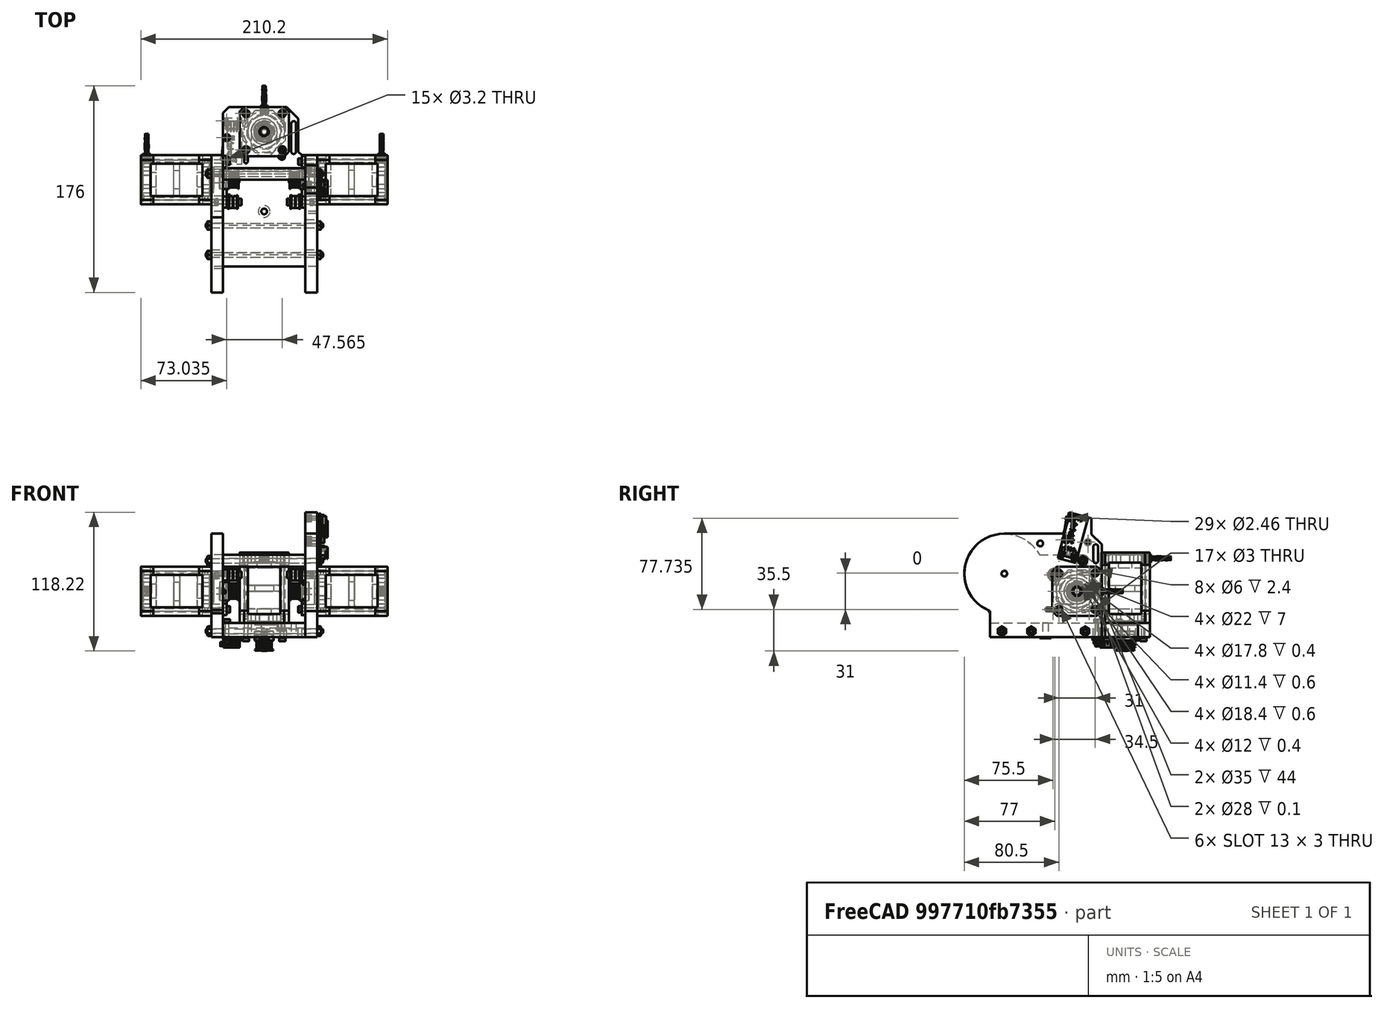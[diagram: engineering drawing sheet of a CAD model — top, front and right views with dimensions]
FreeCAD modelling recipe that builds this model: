
FCSTD DOCUMENT  (FreeCAD 0.20R29410 (Git))
Label: #0_ASSEMBLY_MOTORS_BASE
License: All rights reserved
LicenseURL: http://en.wikipedia.org/wiki/All_rights_reserved
objects: Part::FeaturePython×90, App::FeaturePython×50
note: 90 computed .brp shape members not serialized (recipe doc carries the construction recipe); baked Part::Feature solids carry a one-line shape summary decoded from their .brp

FEATURE [Part::FeaturePython] b__5_MotorsBase_001_  label="#5_MotorsBase_001"  # a2plus imported part (geometry in sourceFile) (typed FeaturePython)
  a2p_Version = 0.4.60k
  fixedPosition = true
  objectType = a2pPart
  sourceFile = .\#5_MotorsBase.FCStd
  subassemblyImport = false
  timeLastImport = 1.68857e+09
  updateColors = true
FEATURE [Part::FeaturePython] b__7_MotorsPlateRight_001_  label="#7_MotorsPlateRight_001"  # a2plus imported part (geometry in sourceFile) (typed FeaturePython)
  Placement = pos=(-35.1,-35,54) rot=(0,0,-1;1.5708rad)
  a2p_Version = 0.4.60k
  fixedPosition = false
  objectType = a2pPart
  sourceFile = .\#7_MotorsPlateRight.FCStd
  subassemblyImport = false
  timeLastImport = 1.68294e+09
  updateColors = true
FEATURE [Part::FeaturePython] b__8_MotorsPlateLeft_001_  label="#8_MotorsPlateLeft_001"  # a2plus imported part (geometry in sourceFile) (typed FeaturePython)
  Placement = pos=(45.1,-35,54) rot=(0,0,-1;1.5708rad)
  a2p_Version = 0.4.60k
  fixedPosition = false
  objectType = a2pPart
  sourceFile = .\#8_MotorsPlateLeft.FCStd
  subassemblyImport = false
  timeLastImport = 1.68302e+09
  updateColors = true
FEATURE [Part::FeaturePython] b__12_MotorsBaseSpacer_001_  label="#12_MotorsBaseSpacer_001"  # a2plus imported part (geometry in sourceFile) (typed FeaturePython)
  Placement = pos=(35.1,32,65) rot=(0,-1,0;1.5708rad)
  a2p_Version = 0.4.60k
  fixedPosition = false
  objectType = a2pPart
  sourceFile = .\#12_MotorsBaseSpacer.FCStd
  subassemblyImport = false
  timeLastImport = 1.68301e+09
  updateColors = true
FEATURE [App::FeaturePython] circularEdge_001  label="circularEdge_001__#5_MotorsBase_001"  # a2plus constraint (typed FeaturePython)
  Object1 = b__8_MotorsPlateLeft_001_
  Object2 = b__5_MotorsBase_001_
  ParentTreeObject = -> b__8_MotorsPlateLeft_001_
  SubElement1 = Edge100
  SubElement2 = Edge71
  Suppressed = false
  Type = circularEdge
  directionConstraint = 1
  lockRotation = false
  offset = 0
FEATURE [App::FeaturePython] circularEdge_001_mirror  label="circularEdge_001__#8_MotorsPlateLeft_001"  # a2plus constraint (typed FeaturePython)
  Object1 = b__8_MotorsPlateLeft_001_
  Object2 = b__5_MotorsBase_001_
  ParentTreeObject = -> b__5_MotorsBase_001_
  SubElement1 = Edge100
  SubElement2 = Edge71
  Suppressed = false
  Type = circularEdge
  directionConstraint = 1
  lockRotation = false
  offset = 0
FEATURE [App::FeaturePython] circularEdge_002  label="circularEdge_002__#5_MotorsBase_001"  # a2plus constraint (typed FeaturePython)
  Object1 = b__7_MotorsPlateRight_001_
  Object2 = b__5_MotorsBase_001_
  ParentTreeObject = -> b__7_MotorsPlateRight_001_
  SubElement1 = Edge32
  SubElement2 = Edge50
  Suppressed = false
  Type = circularEdge
  directionConstraint = 1
  lockRotation = false
  offset = 0
FEATURE [App::FeaturePython] circularEdge_002_mirror  label="circularEdge_002__#7_MotorsPlateRight_001"  # a2plus constraint (typed FeaturePython)
  Object1 = b__7_MotorsPlateRight_001_
  Object2 = b__5_MotorsBase_001_
  ParentTreeObject = -> b__5_MotorsBase_001_
  SubElement1 = Edge32
  SubElement2 = Edge50
  Suppressed = false
  Type = circularEdge
  directionConstraint = 1
  lockRotation = false
  offset = 0
FEATURE [App::FeaturePython] circularEdge_003  label="circularEdge_003__#5_MotorsBase_001"  # a2plus constraint (typed FeaturePython)
  Object1 = b__7_MotorsPlateRight_001_
  Object2 = b__5_MotorsBase_001_
  ParentTreeObject = -> b__7_MotorsPlateRight_001_
  SubElement1 = Edge12
  SubElement2 = Edge45
  Suppressed = false
  Type = circularEdge
  directionConstraint = 1
  lockRotation = false
  offset = 0
FEATURE [App::FeaturePython] circularEdge_003_mirror  label="circularEdge_003__#7_MotorsPlateRight_001"  # a2plus constraint (typed FeaturePython)
  Object1 = b__7_MotorsPlateRight_001_
  Object2 = b__5_MotorsBase_001_
  ParentTreeObject = -> b__5_MotorsBase_001_
  SubElement1 = Edge12
  SubElement2 = Edge45
  Suppressed = false
  Type = circularEdge
  directionConstraint = 1
  lockRotation = false
  offset = 0
FEATURE [App::FeaturePython] circularEdge_004  label="circularEdge_004__#7_MotorsPlateRight_001"  # a2plus constraint (typed FeaturePython)
  Object1 = b__12_MotorsBaseSpacer_001_
  Object2 = b__7_MotorsPlateRight_001_
  ParentTreeObject = -> b__12_MotorsBaseSpacer_001_
  SubElement1 = Edge3
  SubElement2 = Edge25
  Suppressed = false
  Type = circularEdge
  directionConstraint = 0
  lockRotation = false
  offset = 0
FEATURE [App::FeaturePython] circularEdge_004_mirror  label="circularEdge_004__#12_MotorsBaseSpacer_001"  # a2plus constraint (typed FeaturePython)
  Object1 = b__12_MotorsBaseSpacer_001_
  Object2 = b__7_MotorsPlateRight_001_
  ParentTreeObject = -> b__7_MotorsPlateRight_001_
  SubElement1 = Edge3
  SubElement2 = Edge25
  Suppressed = false
  Type = circularEdge
  directionConstraint = 0
  lockRotation = false
  offset = 0
FEATURE [Part::FeaturePython] Nut  label="M4-Tuerca"  # Fasteners workbench fastener (typed FeaturePython)
  Placement = pos=(-45.1,34,5) rot=(0,-1,0;1.5708rad)
  baseObject = -> b__7_MotorsPlateRight_001_ [Edge43]
  diameter = 6
  invert = false
  leftHanded = false
  matchOuter = false
  offset = 0
  thread = false
  type = 22
FEATURE [Part::FeaturePython] Nut001  label="M4-Tuerca001"  # Fasteners workbench fastener (typed FeaturePython)
  Placement = pos=(-45.1,-12,5) rot=(0,-1,0;1.5708rad)
  baseObject = -> b__7_MotorsPlateRight_001_ [Edge67]
  diameter = 6
  invert = false
  leftHanded = false
  matchOuter = false
  offset = 0
  thread = false
  type = 22
FEATURE [Part::FeaturePython] Nut002  label="M4-Tuerca002"  # Fasteners workbench fastener (typed FeaturePython)
  Placement = pos=(-45.1,-37,5) rot=(0,-1,0;1.5708rad)
  baseObject = -> b__7_MotorsPlateRight_001_ [Edge68]
  diameter = 6
  invert = false
  leftHanded = false
  matchOuter = false
  offset = 0
  thread = false
  type = 22
FEATURE [Part::FeaturePython] Nut003  label="M4-Tuerca006"  # Fasteners workbench fastener (typed FeaturePython)
  Placement = pos=(45.1,-37,5) rot=(0,1,0;1.5708rad)
  baseObject = -> b__8_MotorsPlateLeft_001_ [Edge49]
  diameter = 6
  invert = true
  leftHanded = false
  matchOuter = false
  offset = 0
  thread = false
  type = 22
FEATURE [Part::FeaturePython] Nut004  label="M4-Tuerca007"  # Fasteners workbench fastener (typed FeaturePython)
  Placement = pos=(45.1,-12,5) rot=(0,1,0;1.5708rad)
  baseObject = -> b__8_MotorsPlateLeft_001_ [Edge48]
  diameter = 6
  invert = true
  leftHanded = false
  matchOuter = false
  offset = 0
  thread = false
  type = 22
FEATURE [Part::FeaturePython] Nut005  label="M4-Tuerca008"  # Fasteners workbench fastener (typed FeaturePython)
  Placement = pos=(45.1,34,5) rot=(0,1,0;1.5708rad)
  baseObject = -> b__8_MotorsPlateLeft_001_ [Edge21]
  diameter = 6
  invert = true
  leftHanded = false
  matchOuter = false
  offset = 0
  thread = false
  type = 22
FEATURE [Part::FeaturePython] Nut008  label="M3-Tuerca"  # Fasteners workbench fastener (typed FeaturePython)
  Placement = pos=(39.1,8,53) rot=(0,1,0;1.5708rad)
  baseObject = -> b__8_MotorsPlateLeft_001_ [Edge153]
  diameter = 4
  invert = true
  leftHanded = false
  matchOuter = false
  offset = 0
  thread = false
  type = 22
FEATURE [Part::FeaturePython] Nut009  label="M3-Tuerca001"  # Fasteners workbench fastener (typed FeaturePython)
  Placement = pos=(-39.1,8,53) rot=(0,-1,0;1.5708rad)
  baseObject = -> b__7_MotorsPlateRight_001_ [Edge92]
  diameter = 4
  invert = false
  leftHanded = false
  matchOuter = false
  offset = 0
  thread = false
  type = 22
FEATURE [Part::FeaturePython] Nut010  label="M4-Tuerca009"  # Fasteners workbench fastener (typed FeaturePython)
  Placement = pos=(-45.1,32,65) rot=(0,-1,0;1.5708rad)
  baseObject = -> b__7_MotorsPlateRight_001_ [Edge56]
  diameter = 6
  invert = false
  leftHanded = false
  matchOuter = false
  offset = 0
  thread = false
  type = 22
FEATURE [Part::FeaturePython] Nut012  label="M3-Tuerca003"  # Fasteners workbench fastener (typed FeaturePython)
  Placement = pos=(40.1,22.8388,101.235) rot=(0,-1,0;1.5708rad)
  baseObject = -> b__8_MotorsPlateLeft_001_ [Edge146]
  diameter = 4
  invert = false
  leftHanded = false
  matchOuter = false
  offset = 0
  thread = false
  type = 22
FEATURE [Part::FeaturePython] Nut014  label="M3-Tuerca004"  # Fasteners workbench fastener (typed FeaturePython)
  Placement = pos=(40.1,17.9213,82.882) rot=(0,-1,0;1.5708rad)
  baseObject = -> b__8_MotorsPlateLeft_001_ [Edge144]
  diameter = 4
  invert = false
  leftHanded = false
  matchOuter = false
  offset = 0
  thread = false
  type = 22
FEATURE [Part::FeaturePython] Nut015  label="M3-Tuerca005"  # Fasteners workbench fastener (typed FeaturePython)
  Placement = pos=(40.1,36.317,80.8) rot=(0,-1,0;1.5708rad)
  baseObject = -> b__8_MotorsPlateLeft_001_ [Edge130]
  diameter = 4
  invert = false
  leftHanded = false
  matchOuter = false
  offset = 0
  thread = false
  type = 22
FEATURE [Part::FeaturePython] Nut016  label="M3-Tuerca006"  # Fasteners workbench fastener (typed FeaturePython)
  Placement = pos=(14.9991,47.0047,5) rot=(0,0,1;0rad)
  baseObject = -> b__5_MotorsBase_001_ [Edge118]
  diameter = 4
  invert = false
  leftHanded = false
  matchOuter = false
  offset = 0
  thread = false
  type = 22
FEATURE [Part::FeaturePython] ThreadedRod  label="M4x100-Barra roscada"  # Fasteners workbench fastener (typed FeaturePython)
  Placement = pos=(-49.8,34,5) rot=(0,-1,0;1.5708rad)
  baseObject = -> Nut [Edge2]
  diameter = 6
  diameterCustom = 6
  invert = false
  leftHanded = false
  length = 100
  matchOuter = false
  offset = 1.5
  pitchCustom = 1
  thread = false
  type = 4
FEATURE [Part::FeaturePython] Nut017  label="M4-Tuerca012"  # Fasteners workbench fastener (typed FeaturePython)
  Placement = pos=(-45.1,34,5) rot=(0,-1,0;1.5708rad)
  diameter = 6
  invert = false
  leftHanded = false
  matchOuter = false
  offset = 0
  thread = false
  type = 22
FEATURE [Part::FeaturePython] ThreadedRod001  label="M4x100-Barra roscada001"  # Fasteners workbench fastener (typed FeaturePython)
  Placement = pos=(-49.8,-12,5) rot=(0,-1,0;1.5708rad)
  baseObject = -> Nut001 [Edge2]
  diameter = 6
  diameterCustom = 6
  invert = false
  leftHanded = false
  length = 100
  matchOuter = false
  offset = 1.5
  pitchCustom = 1
  thread = false
  type = 4
FEATURE [Part::FeaturePython] ThreadedRod002  label="M4x100-Barra roscada002"  # Fasteners workbench fastener (typed FeaturePython)
  Placement = pos=(-49.8,-37,5) rot=(0,-1,0;1.5708rad)
  baseObject = -> Nut002 [Edge2]
  diameter = 6
  diameterCustom = 6
  invert = false
  leftHanded = false
  length = 100
  matchOuter = false
  offset = 1.5
  pitchCustom = 1
  thread = false
  type = 4
FEATURE [Part::FeaturePython] ThreadedRod003  label="M4x100-Barra roscada003"  # Fasteners workbench fastener (typed FeaturePython)
  Placement = pos=(-49.8,32,65) rot=(0,-1,0;1.5708rad)
  baseObject = -> Nut010 [Edge2]
  diameter = 6
  diameterCustom = 6
  invert = false
  leftHanded = false
  length = 100
  matchOuter = false
  offset = 1.5
  pitchCustom = 1
  thread = false
  type = 4
FEATURE [Part::FeaturePython] Nut018  label="M4-Tuerca011"  # Fasteners workbench fastener (typed FeaturePython)
  Placement = pos=(45.1,32,65) rot=(0,1,0;1.5708rad)
  baseObject = -> b__8_MotorsPlateLeft_001_ [Edge38]
  diameter = 6
  invert = true
  leftHanded = false
  matchOuter = false
  offset = 0
  thread = false
  type = 22
FEATURE [Part::FeaturePython] Washer  label="M5-Arandela"  # Fasteners workbench fastener (typed FeaturePython)
  Placement = pos=(0,0,0) rot=(1,0,0;3.14159rad)
  baseObject = -> b__5_MotorsBase_001_ [Edge10]
  diameter = 6
  invert = true
  matchOuter = false
  offset = 0
  type = 4
FEATURE [Part::FeaturePython] b__22_MotorsSlider_001_  label="#22_MotorsSlider_001"  # a2plus imported part (geometry in sourceFile) (typed FeaturePython)
  Placement = pos=(-32.1,42.5,23.5) rot=(0.57735,-0.57735,-0.57735;2.0944rad)
  a2p_Version = 0.4.60k
  fixedPosition = false
  objectType = a2pPart
  sourceFile = .\#22_MotorsSlider.FCStd
  subassemblyImport = false
  timeLastImport = 1.68302e+09
  updateColors = true
FEATURE [Part::FeaturePython] b__22_MotorsSlider_001_001  label="#22_MotorsSlider_002"  # a2plus imported part (geometry in sourceFile) (typed FeaturePython)
  Placement = pos=(35.1,42.5,23.5) rot=(0.57735,-0.57735,-0.57735;2.0944rad)
  a2p_Version = 0.4.60k
  fixedPosition = false
  objectType = a2pPart
  sourceFile = .\#22_MotorsSlider.FCStd
  subassemblyImport = false
  timeLastImport = 1.68302e+09
  updateColors = true
FEATURE [App::FeaturePython] circularEdge_005  label="circularEdge_005__#8_MotorsPlateLeft_001"  # a2plus constraint (typed FeaturePython)
  Object1 = b__22_MotorsSlider_001_001
  Object2 = b__8_MotorsPlateLeft_001_
  ParentTreeObject = -> b__22_MotorsSlider_001_001
  SubElement1 = Edge14
  SubElement2 = Edge74
  Suppressed = false
  Type = circularEdge
  directionConstraint = 0
  lockRotation = false
  offset = 0
FEATURE [App::FeaturePython] circularEdge_005_mirror  label="circularEdge_005__#22_MotorsSlider_002"  # a2plus constraint (typed FeaturePython)
  Object1 = b__22_MotorsSlider_001_001
  Object2 = b__8_MotorsPlateLeft_001_
  ParentTreeObject = -> b__8_MotorsPlateLeft_001_
  SubElement1 = Edge14
  SubElement2 = Edge74
  Suppressed = false
  Type = circularEdge
  directionConstraint = 0
  lockRotation = false
  offset = 0
FEATURE [App::FeaturePython] circularEdge_006  label="circularEdge_006__#8_MotorsPlateLeft_001"  # a2plus constraint (typed FeaturePython)
  Object1 = b__22_MotorsSlider_001_001
  Object2 = b__8_MotorsPlateLeft_001_
  ParentTreeObject = -> b__22_MotorsSlider_001_001
  SubElement1 = Edge12
  SubElement2 = Edge65
  Suppressed = false
  Type = circularEdge
  directionConstraint = 0
  lockRotation = false
  offset = 0
FEATURE [App::FeaturePython] circularEdge_006_mirror  label="circularEdge_006__#22_MotorsSlider_002"  # a2plus constraint (typed FeaturePython)
  Object1 = b__22_MotorsSlider_001_001
  Object2 = b__8_MotorsPlateLeft_001_
  ParentTreeObject = -> b__8_MotorsPlateLeft_001_
  SubElement1 = Edge12
  SubElement2 = Edge65
  Suppressed = false
  Type = circularEdge
  directionConstraint = 0
  lockRotation = false
  offset = 0
FEATURE [App::FeaturePython] circularEdge_007  label="circularEdge_007__#7_MotorsPlateRight_001"  # a2plus constraint (typed FeaturePython)
  Object1 = b__22_MotorsSlider_001_
  Object2 = b__7_MotorsPlateRight_001_
  ParentTreeObject = -> b__22_MotorsSlider_001_
  SubElement1 = Edge25
  SubElement2 = Edge14
  Suppressed = false
  Type = circularEdge
  directionConstraint = 0
  lockRotation = false
  offset = 0
FEATURE [App::FeaturePython] circularEdge_007_mirror  label="circularEdge_007__#22_MotorsSlider_001"  # a2plus constraint (typed FeaturePython)
  Object1 = b__22_MotorsSlider_001_
  Object2 = b__7_MotorsPlateRight_001_
  ParentTreeObject = -> b__7_MotorsPlateRight_001_
  SubElement1 = Edge25
  SubElement2 = Edge14
  Suppressed = false
  Type = circularEdge
  directionConstraint = 0
  lockRotation = false
  offset = 0
FEATURE [App::FeaturePython] circularEdge_008  label="circularEdge_008__#7_MotorsPlateRight_001"  # a2plus constraint (typed FeaturePython)
  Object1 = b__22_MotorsSlider_001_
  Object2 = b__7_MotorsPlateRight_001_
  ParentTreeObject = -> b__22_MotorsSlider_001_
  SubElement1 = Edge24
  SubElement2 = Edge18
  Suppressed = false
  Type = circularEdge
  directionConstraint = 0
  lockRotation = false
  offset = 0
FEATURE [App::FeaturePython] circularEdge_008_mirror  label="circularEdge_008__#22_MotorsSlider_001"  # a2plus constraint (typed FeaturePython)
  Object1 = b__22_MotorsSlider_001_
  Object2 = b__7_MotorsPlateRight_001_
  ParentTreeObject = -> b__7_MotorsPlateRight_001_
  SubElement1 = Edge24
  SubElement2 = Edge18
  Suppressed = false
  Type = circularEdge
  directionConstraint = 0
  lockRotation = false
  offset = 0
FEATURE [Part::FeaturePython] Screw  label="M3x16-Tornillo"  # Fasteners workbench fastener (typed FeaturePython)
  Placement = pos=(32.1,42.5,54.5) rot=(0,-1,0;1.5708rad)
  baseObject = -> b__22_MotorsSlider_001_001 [Edge26]
  diameter = 4
  invert = false
  leftHanded = false
  length = 10
  lengthCustom = 16
  matchOuter = false
  offset = 0
  thread = false
  type = 45
FEATURE [Part::FeaturePython] Screw001  label="M3x16-Tornillo001"  # Fasteners workbench fastener (typed FeaturePython)
  Placement = pos=(32.1,11.5,23.5) rot=(0,-1,0;1.5708rad)
  baseObject = -> b__22_MotorsSlider_001_001 [Edge24]
  diameter = 4
  invert = false
  leftHanded = false
  length = 10
  lengthCustom = 16
  matchOuter = false
  offset = 0
  thread = false
  type = 45
FEATURE [Part::FeaturePython] Screw002  label="M3x16-Tornillo002"  # Fasteners workbench fastener (typed FeaturePython)
  Placement = pos=(32.1,42.5,23.5) rot=(0,-1,0;1.5708rad)
  baseObject = -> b__22_MotorsSlider_001_001 [Edge25]
  diameter = 4
  invert = false
  leftHanded = false
  length = 10
  lengthCustom = 16
  matchOuter = false
  offset = 0
  thread = false
  type = 45
FEATURE [Part::FeaturePython] Screw003  label="M3x16-Tornillo006"  # Fasteners workbench fastener (typed FeaturePython)
  Placement = pos=(-32.1,11.5,23.5) rot=(0,1,0;1.5708rad)
  baseObject = -> b__22_MotorsSlider_001_ [Edge12]
  diameter = 4
  invert = true
  leftHanded = false
  length = 10
  lengthCustom = 16
  matchOuter = false
  offset = 0
  thread = false
  type = 45
FEATURE [Part::FeaturePython] Screw004  label="M3x16-Tornillo007"  # Fasteners workbench fastener (typed FeaturePython)
  Placement = pos=(-32.1,42.5,23.5) rot=(0,1,0;1.5708rad)
  baseObject = -> b__22_MotorsSlider_001_ [Edge13]
  diameter = 4
  invert = true
  leftHanded = false
  length = 10
  lengthCustom = 16
  matchOuter = false
  offset = 0
  thread = false
  type = 45
FEATURE [Part::FeaturePython] Screw005  label="M3x16-Tornillo008"  # Fasteners workbench fastener (typed FeaturePython)
  Placement = pos=(-32.1,42.5,54.5) rot=(0,1,0;1.5708rad)
  baseObject = -> b__22_MotorsSlider_001_ [Edge14]
  diameter = 4
  invert = true
  leftHanded = false
  length = 10
  lengthCustom = 16
  matchOuter = false
  offset = 0
  thread = false
  type = 45
FEATURE [Part::FeaturePython] b_NEMA171_001_  label="NEMA171_001"  # a2plus imported part (geometry in sourceFile) (typed FeaturePython)
  Placement = pos=(-45.1,27,39) rot=(-0.57735,0.57735,0.57735;2.0944rad)
  a2p_Version = 0.4.60k
  fixedPosition = false
  objectType = a2pPart
  sourceFile = .\..\Complements\NEMA17.step
  subassemblyImport = false
  timeLastImport = 1.68865e+09
  updateColors = true
FEATURE [Part::FeaturePython] b_NEMA171_001_001  label="NEMA171_002"  # a2plus imported part (geometry in sourceFile) (typed FeaturePython)
  Placement = pos=(45.1,27,39) rot=(-0.57735,-0.57735,-0.57735;2.0944rad)
  a2p_Version = 0.4.60k
  fixedPosition = false
  objectType = a2pPart
  sourceFile = .\..\Complements\NEMA17.step
  subassemblyImport = false
  timeLastImport = 1.68865e+09
  updateColors = true
FEATURE [App::FeaturePython] circularEdge_009  label="circularEdge_009__#8_MotorsPlateLeft_001"  # a2plus constraint (typed FeaturePython)
  Object1 = b_NEMA171_001_001
  Object2 = b__8_MotorsPlateLeft_001_
  ParentTreeObject = -> b_NEMA171_001_001
  SubElement1 = Edge722
  SubElement2 = Edge27
  Suppressed = false
  Type = circularEdge
  directionConstraint = 0
  lockRotation = false
  offset = 0
FEATURE [App::FeaturePython] circularEdge_009_mirror  label="circularEdge_009__NEMA171_002"  # a2plus constraint (typed FeaturePython)
  Object1 = b_NEMA171_001_001
  Object2 = b__8_MotorsPlateLeft_001_
  ParentTreeObject = -> b__8_MotorsPlateLeft_001_
  SubElement1 = Edge722
  SubElement2 = Edge27
  Suppressed = false
  Type = circularEdge
  directionConstraint = 0
  lockRotation = false
  offset = 0
FEATURE [App::FeaturePython] circularEdge_010  label="circularEdge_010__#7_MotorsPlateRight_001"  # a2plus constraint (typed FeaturePython)
  Object1 = b_NEMA171_001_
  Object2 = b__7_MotorsPlateRight_001_
  ParentTreeObject = -> b_NEMA171_001_
  SubElement1 = Edge722
  SubElement2 = Edge59
  Suppressed = false
  Type = circularEdge
  directionConstraint = 1
  lockRotation = false
  offset = 0
FEATURE [App::FeaturePython] circularEdge_010_mirror  label="circularEdge_010__NEMA171_001"  # a2plus constraint (typed FeaturePython)
  Object1 = b_NEMA171_001_
  Object2 = b__7_MotorsPlateRight_001_
  ParentTreeObject = -> b__7_MotorsPlateRight_001_
  SubElement1 = Edge722
  SubElement2 = Edge59
  Suppressed = false
  Type = circularEdge
  directionConstraint = 1
  lockRotation = false
  offset = 0
FEATURE [App::FeaturePython] circularEdge_011  label="circularEdge_011__#7_MotorsPlateRight_001"  # a2plus constraint (typed FeaturePython)
  Object1 = b_NEMA171_001_
  Object2 = b__7_MotorsPlateRight_001_
  ParentTreeObject = -> b_NEMA171_001_
  SubElement1 = Edge720
  SubElement2 = Edge54
  Suppressed = false
  Type = circularEdge
  directionConstraint = 1
  lockRotation = false
  offset = 0
FEATURE [App::FeaturePython] circularEdge_011_mirror  label="circularEdge_011__NEMA171_001"  # a2plus constraint (typed FeaturePython)
  Object1 = b_NEMA171_001_
  Object2 = b__7_MotorsPlateRight_001_
  ParentTreeObject = -> b__7_MotorsPlateRight_001_
  SubElement1 = Edge720
  SubElement2 = Edge54
  Suppressed = false
  Type = circularEdge
  directionConstraint = 1
  lockRotation = false
  offset = 0
FEATURE [App::FeaturePython] circularEdge_012  label="circularEdge_012__#8_MotorsPlateLeft_001"  # a2plus constraint (typed FeaturePython)
  Object1 = b_NEMA171_001_001
  Object2 = b__8_MotorsPlateLeft_001_
  ParentTreeObject = -> b_NEMA171_001_001
  SubElement1 = Edge723
  SubElement2 = Edge31
  Suppressed = false
  Type = circularEdge
  directionConstraint = 0
  lockRotation = false
  offset = 0
FEATURE [App::FeaturePython] circularEdge_012_mirror  label="circularEdge_012__NEMA171_002"  # a2plus constraint (typed FeaturePython)
  Object1 = b_NEMA171_001_001
  Object2 = b__8_MotorsPlateLeft_001_
  ParentTreeObject = -> b__8_MotorsPlateLeft_001_
  SubElement1 = Edge723
  SubElement2 = Edge31
  Suppressed = false
  Type = circularEdge
  directionConstraint = 0
  lockRotation = false
  offset = 0
FEATURE [Part::FeaturePython] b_GT2_20T1_001_  label="GT2_20T1_001"  # a2plus imported part (geometry in sourceFile) (typed FeaturePython)
  Placement = pos=(-38.1,27,39) rot=(0.501609,0.704824,0.501609;1.91368rad)
  a2p_Version = 0.4.60k
  fixedPosition = false
  objectType = a2pPart
  sourceFile = .\..\Complements\GT2_20T.step
  subassemblyImport = false
  timeLastImport = 1.68865e+09
  updateColors = true
FEATURE [Part::FeaturePython] b_GT2_20T1_001_001  label="GT2_20T1_002"  # a2plus imported part (geometry in sourceFile) (typed FeaturePython)
  Placement = pos=(38.1,27,39) rot=(0,-1,0;1.5708rad)
  a2p_Version = 0.4.60k
  fixedPosition = false
  objectType = a2pPart
  sourceFile = .\..\Complements\GT2_20T.step
  subassemblyImport = false
  timeLastImport = 1.68865e+09
  updateColors = true
FEATURE [App::FeaturePython] circularEdge_013  label="circularEdge_013__NEMA171_002"  # a2plus constraint (typed FeaturePython)
  Object1 = b_GT2_20T1_001_001
  Object2 = b_NEMA171_001_001
  ParentTreeObject = -> b_GT2_20T1_001_001
  SubElement1 = Edge38
  SubElement2 = Edge1361
  Suppressed = false
  Type = circularEdge
  directionConstraint = 1
  lockRotation = false
  offset = -2
FEATURE [App::FeaturePython] circularEdge_013_mirror  label="circularEdge_013__GT2_20T1_002"  # a2plus constraint (typed FeaturePython)
  Object1 = b_GT2_20T1_001_001
  Object2 = b_NEMA171_001_001
  ParentTreeObject = -> b_NEMA171_001_001
  SubElement1 = Edge38
  SubElement2 = Edge1361
  Suppressed = false
  Type = circularEdge
  directionConstraint = 1
  lockRotation = false
  offset = -2
FEATURE [App::FeaturePython] circularEdge_014  label="circularEdge_014__NEMA171_001"  # a2plus constraint (typed FeaturePython)
  Object1 = b_GT2_20T1_001_
  Object2 = b_NEMA171_001_
  ParentTreeObject = -> b_GT2_20T1_001_
  SubElement1 = Edge38
  SubElement2 = Edge1361
  Suppressed = false
  Type = circularEdge
  directionConstraint = 1
  lockRotation = false
  offset = -2
FEATURE [App::FeaturePython] circularEdge_014_mirror  label="circularEdge_014__GT2_20T1_001"  # a2plus constraint (typed FeaturePython)
  Object1 = b_GT2_20T1_001_
  Object2 = b_NEMA171_001_
  ParentTreeObject = -> b_NEMA171_001_
  SubElement1 = Edge38
  SubElement2 = Edge1361
  Suppressed = false
  Type = circularEdge
  directionConstraint = 1
  lockRotation = false
  offset = -2
FEATURE [Part::FeaturePython] b_NEMA171_001_002  label="NEMA171_003"  # a2plus imported part (geometry in sourceFile) (typed FeaturePython)
  Placement = pos=(-1.82486e-07,68,12) rot=(0,0.707107,0.707107;3.14159rad)
  a2p_Version = 0.4.60k
  fixedPosition = false
  objectType = a2pPart
  sourceFile = .\..\Complements\NEMA17.step
  subassemblyImport = false
  timeLastImport = 1.68865e+09
  updateColors = true
FEATURE [Part::FeaturePython] b_GT2_20T1_001_002  label="GT2_20T1_003"  # a2plus imported part (geometry in sourceFile) (typed FeaturePython)
  Placement = pos=(-1.82331e-07,68,5) rot=(0.855543,0.517732,0;3.14159rad)
  a2p_Version = 0.4.60k
  fixedPosition = false
  objectType = a2pPart
  sourceFile = .\..\Complements\GT2_20T.step
  subassemblyImport = false
  timeLastImport = 1.68865e+09
  updateColors = true
FEATURE [App::FeaturePython] circularEdge_015  label="circularEdge_015__#5_MotorsBase_001"  # a2plus constraint (typed FeaturePython)
  Object1 = b_NEMA171_001_002
  Object2 = b__5_MotorsBase_001_
  ParentTreeObject = -> b_NEMA171_001_002
  SubElement1 = Edge722
  SubElement2 = Edge110
  Suppressed = false
  Type = circularEdge
  directionConstraint = 1
  lockRotation = false
  offset = 0
FEATURE [App::FeaturePython] circularEdge_015_mirror  label="circularEdge_015__NEMA171_003"  # a2plus constraint (typed FeaturePython)
  Object1 = b_NEMA171_001_002
  Object2 = b__5_MotorsBase_001_
  ParentTreeObject = -> b__5_MotorsBase_001_
  SubElement1 = Edge722
  SubElement2 = Edge110
  Suppressed = false
  Type = circularEdge
  directionConstraint = 1
  lockRotation = false
  offset = 0
FEATURE [App::FeaturePython] circularEdge_016  label="circularEdge_016__#5_MotorsBase_001"  # a2plus constraint (typed FeaturePython)
  Object1 = b_NEMA171_001_002
  Object2 = b__5_MotorsBase_001_
  ParentTreeObject = -> b_NEMA171_001_002
  SubElement1 = Edge723
  SubElement2 = Edge102
  Suppressed = false
  Type = circularEdge
  directionConstraint = 1
  lockRotation = false
  offset = 0
FEATURE [App::FeaturePython] circularEdge_016_mirror  label="circularEdge_016__NEMA171_003"  # a2plus constraint (typed FeaturePython)
  Object1 = b_NEMA171_001_002
  Object2 = b__5_MotorsBase_001_
  ParentTreeObject = -> b__5_MotorsBase_001_
  SubElement1 = Edge723
  SubElement2 = Edge102
  Suppressed = false
  Type = circularEdge
  directionConstraint = 1
  lockRotation = false
  offset = 0
FEATURE [Part::FeaturePython] Washer001  label="M3-Arandela"  # Fasteners workbench fastener (typed FeaturePython)
  Placement = pos=(15.5,83.5,0) rot=(1,0,0;3.14159rad)
  baseObject = -> b__5_MotorsBase_001_ [Edge30]
  diameter = 4
  invert = true
  matchOuter = false
  offset = 0
  type = 4
FEATURE [Part::FeaturePython] Washer002  label="M3-Arandela003"  # Fasteners workbench fastener (typed FeaturePython)
  Placement = pos=(-15.5,83.5,0) rot=(1,0,0;3.14159rad)
  baseObject = -> b__5_MotorsBase_001_ [Edge17]
  diameter = 4
  invert = true
  matchOuter = false
  offset = 0
  type = 4
FEATURE [Part::FeaturePython] Washer003  label="M3-Arandela004"  # Fasteners workbench fastener (typed FeaturePython)
  Placement = pos=(-15.5,52.5,0) rot=(1,0,0;3.14159rad)
  baseObject = -> b__5_MotorsBase_001_ [Edge13]
  diameter = 4
  invert = true
  matchOuter = false
  offset = 0
  type = 4
FEATURE [Part::FeaturePython] Screw006  label="M3x16-Tornillo009"  # Fasteners workbench fastener (typed FeaturePython)
  Placement = pos=(15.5,83.5,-0.5) rot=(1,0,0;3.14159rad)
  baseObject = -> Washer001 [Edge1]
  diameter = 4
  invert = false
  leftHanded = false
  length = 10
  lengthCustom = 16
  matchOuter = false
  offset = 0
  thread = false
  type = 45
FEATURE [Part::FeaturePython] Screw007  label="M3x16-Tornillo010"  # Fasteners workbench fastener (typed FeaturePython)
  Placement = pos=(-15.5,83.5,-0.5) rot=(1,0,0;3.14159rad)
  baseObject = -> Washer002 [Edge1]
  diameter = 4
  invert = false
  leftHanded = false
  length = 10
  lengthCustom = 16
  matchOuter = false
  offset = 0
  thread = false
  type = 45
FEATURE [Part::FeaturePython] Screw008  label="M3x16-Tornillo011"  # Fasteners workbench fastener (typed FeaturePython)
  Placement = pos=(-15.5,52.5,-0.5) rot=(1,0,0;3.14159rad)
  baseObject = -> Washer003 [Edge1]
  diameter = 4
  invert = false
  leftHanded = false
  length = 10
  lengthCustom = 16
  matchOuter = false
  offset = 0
  thread = false
  type = 45
FEATURE [App::FeaturePython] circularEdge_017  label="circularEdge_017__NEMA171_003"  # a2plus constraint (typed FeaturePython)
  Object1 = b_GT2_20T1_001_002
  Object2 = b_NEMA171_001_002
  ParentTreeObject = -> b_GT2_20T1_001_002
  SubElement1 = Edge37
  SubElement2 = Edge1361
  Suppressed = false
  Type = circularEdge
  directionConstraint = 0
  lockRotation = false
  offset = 2
FEATURE [App::FeaturePython] circularEdge_017_mirror  label="circularEdge_017__GT2_20T1_003"  # a2plus constraint (typed FeaturePython)
  Object1 = b_GT2_20T1_001_002
  Object2 = b_NEMA171_001_002
  ParentTreeObject = -> b_NEMA171_001_002
  SubElement1 = Edge37
  SubElement2 = Edge1361
  Suppressed = false
  Type = circularEdge
  directionConstraint = 0
  lockRotation = false
  offset = 2
FEATURE [Part::FeaturePython] b_Endstop1_001_  label="Endstop1_001"  # a2plus imported part (geometry in sourceFile) (typed FeaturePython)
  Placement = pos=(-26.78,59.1,-2) rot=(0,0,1;1.5708rad)
  a2p_Version = 0.4.60k
  fixedPosition = false
  objectType = a2pPart
  sourceFile = .\..\Complements\Endstop.step
  subassemblyImport = false
  timeLastImport = 1.68866e+09
  updateColors = true
FEATURE [Part::FeaturePython] Washer004  label="M3-Arandela005"  # Fasteners workbench fastener (typed FeaturePython)
  Placement = pos=(-31.78,62.85,0) rot=(1,0,0;3.14159rad)
  baseObject = -> b__5_MotorsBase_001_ [Edge12]
  diameter = 4
  invert = true
  matchOuter = false
  offset = 0
  type = 4
FEATURE [Part::FeaturePython] Washer005  label="M3-Arandela006"  # Fasteners workbench fastener (typed FeaturePython)
  Placement = pos=(-31.78,43.85,0) rot=(1,0,0;3.14159rad)
  baseObject = -> b__5_MotorsBase_001_ [Edge11]
  diameter = 4
  invert = true
  matchOuter = false
  offset = 0
  type = 4
FEATURE [Part::FeaturePython] Washer006  label="M3-Arandela007"  # Fasteners workbench fastener (typed FeaturePython)
  Placement = pos=(-31.78,62.85,-0.5) rot=(1,0,0;3.14159rad)
  baseObject = -> Washer004 [Edge1]
  diameter = 4
  invert = false
  matchOuter = false
  offset = 0
  type = 4
FEATURE [Part::FeaturePython] Washer007  label="M3-Arandela008"  # Fasteners workbench fastener (typed FeaturePython)
  Placement = pos=(-31.78,43.85,-0.5) rot=(1,0,0;3.14159rad)
  baseObject = -> Washer005 [Edge1]
  diameter = 4
  invert = false
  matchOuter = false
  offset = 0
  type = 4
FEATURE [Part::FeaturePython] Washer008  label="M3-Arandela009"  # Fasteners workbench fastener (typed FeaturePython)
  Placement = pos=(-31.78,62.85,-0.5) rot=(1,0,0;3.14159rad)
  baseObject = -> Washer004 [Edge1]
  diameter = 4
  invert = false
  matchOuter = false
  offset = 0
  type = 4
FEATURE [Part::FeaturePython] Washer009  label="M3-Arandela010"  # Fasteners workbench fastener (typed FeaturePython)
  Placement = pos=(-31.78,43.85,-0.5) rot=(1,0,0;3.14159rad)
  baseObject = -> Washer005 [Edge1]
  diameter = 4
  invert = false
  matchOuter = false
  offset = 0
  type = 4
FEATURE [Part::FeaturePython] Washer010  label="M3-Arandela011"  # Fasteners workbench fastener (typed FeaturePython)
  Placement = pos=(-31.78,62.85,-1) rot=(1,0,0;3.14159rad)
  baseObject = -> Washer006 [Edge1]
  diameter = 4
  invert = false
  matchOuter = false
  offset = 0
  type = 4
FEATURE [Part::FeaturePython] Washer011  label="M3-Arandela012"  # Fasteners workbench fastener (typed FeaturePython)
  Placement = pos=(-31.78,43.85,-1) rot=(1,0,0;3.14159rad)
  baseObject = -> Washer007 [Edge1]
  diameter = 4
  invert = false
  matchOuter = false
  offset = 0
  type = 4
FEATURE [Part::FeaturePython] Washer012  label="M3-Arandela013"  # Fasteners workbench fastener (typed FeaturePython)
  Placement = pos=(-31.78,62.85,-0.5) rot=(1,0,0;3.14159rad)
  baseObject = -> Washer004 [Edge1]
  diameter = 4
  invert = false
  matchOuter = false
  offset = 0
  type = 4
FEATURE [Part::FeaturePython] Washer013  label="M3-Arandela014"  # Fasteners workbench fastener (typed FeaturePython)
  Placement = pos=(-31.78,43.85,-0.5) rot=(1,0,0;3.14159rad)
  baseObject = -> Washer005 [Edge1]
  diameter = 4
  invert = false
  matchOuter = false
  offset = 0
  type = 4
FEATURE [Part::FeaturePython] Washer014  label="M3-Arandela015"  # Fasteners workbench fastener (typed FeaturePython)
  Placement = pos=(-31.78,62.85,-1) rot=(1,0,0;3.14159rad)
  baseObject = -> Washer006 [Edge1]
  diameter = 4
  invert = false
  matchOuter = false
  offset = 0
  type = 4
FEATURE [Part::FeaturePython] Washer015  label="M3-Arandela016"  # Fasteners workbench fastener (typed FeaturePython)
  Placement = pos=(-31.78,43.85,-1) rot=(1,0,0;3.14159rad)
  baseObject = -> Washer007 [Edge1]
  diameter = 4
  invert = false
  matchOuter = false
  offset = 0
  type = 4
FEATURE [Part::FeaturePython] Washer016  label="M3-Arandela021"  # Fasteners workbench fastener (typed FeaturePython)
  Placement = pos=(-31.78,62.85,-1.5) rot=(1,0,0;3.14159rad)
  baseObject = -> Washer010 [Edge1]
  diameter = 4
  invert = false
  matchOuter = false
  offset = 0
  type = 4
FEATURE [Part::FeaturePython] Washer017  label="M3-Arandela020"  # Fasteners workbench fastener (typed FeaturePython)
  Placement = pos=(-31.78,43.85,-1.5) rot=(1,0,0;3.14159rad)
  baseObject = -> Washer011 [Edge1]
  diameter = 4
  invert = false
  matchOuter = false
  offset = 0
  type = 4
FEATURE [App::FeaturePython] circularEdge_018  label="circularEdge_018__#5_MotorsBase_001"  # a2plus constraint (typed FeaturePython)
  Object1 = b_Endstop1_001_
  Object2 = b__5_MotorsBase_001_
  ParentTreeObject = -> b_Endstop1_001_
  SubElement1 = Edge459
  SubElement2 = Edge11
  Suppressed = false
  Type = circularEdge
  directionConstraint = 1
  lockRotation = false
  offset = 2
FEATURE [App::FeaturePython] circularEdge_018_mirror  label="circularEdge_018__Endstop1_001"  # a2plus constraint (typed FeaturePython)
  Object1 = b_Endstop1_001_
  Object2 = b__5_MotorsBase_001_
  ParentTreeObject = -> b__5_MotorsBase_001_
  SubElement1 = Edge459
  SubElement2 = Edge11
  Suppressed = false
  Type = circularEdge
  directionConstraint = 1
  lockRotation = false
  offset = 2
FEATURE [Part::FeaturePython] Screw009  label="M3x20-Tornillo"  # Fasteners workbench fastener (typed FeaturePython)
  Placement = pos=(-31.78,62.85,12) rot=(0,0,1;0rad)
  baseObject = -> b__5_MotorsBase_001_ [Edge92]
  diameter = 4
  invert = false
  leftHanded = false
  length = 10
  lengthCustom = 20
  matchOuter = false
  offset = 0
  thread = false
  type = 45
FEATURE [Part::FeaturePython] Screw010  label="M3x20-Tornillo001"  # Fasteners workbench fastener (typed FeaturePython)
  Placement = pos=(-31.78,43.85,12) rot=(0,0,1;0rad)
  baseObject = -> b__5_MotorsBase_001_ [Edge90]
  diameter = 4
  invert = false
  leftHanded = false
  length = 10
  lengthCustom = 20
  matchOuter = false
  offset = 0
  thread = false
  type = 45
FEATURE [Part::FeaturePython] Nut019  label="M3-Tuerca007"  # Fasteners workbench fastener (typed FeaturePython)
  Placement = pos=(-31.78,62.85,-3) rot=(1,0,0;3.14159rad)
  baseObject = -> b_Endstop1_001_ [Edge450]
  diameter = 4
  invert = true
  leftHanded = false
  matchOuter = false
  offset = 0
  thread = false
  type = 22
FEATURE [Part::FeaturePython] Nut020  label="M3-Tuerca008"  # Fasteners workbench fastener (typed FeaturePython)
  Placement = pos=(-31.78,43.85,-3) rot=(1,0,0;3.14159rad)
  baseObject = -> b_Endstop1_001_ [Edge451]
  diameter = 4
  invert = true
  leftHanded = false
  matchOuter = false
  offset = 0
  thread = false
  type = 22
FEATURE [Part::FeaturePython] Washer018  label="M3-Arandela024"  # Fasteners workbench fastener (typed FeaturePython)
  Placement = pos=(45.1,17.9213,82.882) rot=(0,1,0;1.5708rad)
  baseObject = -> b__8_MotorsPlateLeft_001_ [Edge46]
  diameter = 4
  invert = true
  matchOuter = false
  offset = 0
  type = 4
FEATURE [Part::FeaturePython] Washer019  label="M3-Arandela025"  # Fasteners workbench fastener (typed FeaturePython)
  Placement = pos=(45.1,22.8388,101.235) rot=(0,1,0;1.5708rad)
  baseObject = -> b__8_MotorsPlateLeft_001_ [Edge47]
  diameter = 4
  invert = true
  matchOuter = false
  offset = 0
  type = 4
FEATURE [Part::FeaturePython] Washer020  label="M3-Arandela026"  # Fasteners workbench fastener (typed FeaturePython)
  Placement = pos=(45.6,22.8388,101.235) rot=(0,1,0;1.5708rad)
  baseObject = -> Washer019 [Edge1]
  diameter = 4
  invert = false
  matchOuter = false
  offset = 0
  type = 4
FEATURE [Part::FeaturePython] Washer021  label="M3-Arandela027"  # Fasteners workbench fastener (typed FeaturePython)
  Placement = pos=(45.6,17.9213,82.882) rot=(0,1,0;1.5708rad)
  baseObject = -> Washer018 [Edge1]
  diameter = 4
  invert = false
  matchOuter = false
  offset = 0
  type = 4
FEATURE [Part::FeaturePython] Washer022  label="M3-Arandela028"  # Fasteners workbench fastener (typed FeaturePython)
  Placement = pos=(45.6,22.8388,101.235) rot=(0,1,0;1.5708rad)
  baseObject = -> Washer019 [Edge1]
  diameter = 4
  invert = false
  matchOuter = false
  offset = 0
  type = 4
FEATURE [Part::FeaturePython] Washer023  label="M3-Arandela029"  # Fasteners workbench fastener (typed FeaturePython)
  Placement = pos=(45.6,17.9213,82.882) rot=(0,1,0;1.5708rad)
  baseObject = -> Washer018 [Edge1]
  diameter = 4
  invert = false
  matchOuter = false
  offset = 0
  type = 4
FEATURE [Part::FeaturePython] Washer024  label="M3-Arandela030"  # Fasteners workbench fastener (typed FeaturePython)
  Placement = pos=(46.1,22.8388,101.235) rot=(0,1,0;1.5708rad)
  baseObject = -> Washer020 [Edge1]
  diameter = 4
  invert = false
  matchOuter = false
  offset = 0
  type = 4
FEATURE [Part::FeaturePython] Washer025  label="M3-Arandela031"  # Fasteners workbench fastener (typed FeaturePython)
  Placement = pos=(46.1,17.9213,82.882) rot=(0,1,0;1.5708rad)
  baseObject = -> Washer021 [Edge1]
  diameter = 4
  invert = false
  matchOuter = false
  offset = 0
  type = 4
FEATURE [Part::FeaturePython] Washer026  label="M3-Arandela032"  # Fasteners workbench fastener (typed FeaturePython)
  Placement = pos=(45.6,22.8388,101.235) rot=(0,1,0;1.5708rad)
  baseObject = -> Washer019 [Edge1]
  diameter = 4
  invert = false
  matchOuter = false
  offset = 0
  type = 4
FEATURE [Part::FeaturePython] Washer027  label="M3-Arandela033"  # Fasteners workbench fastener (typed FeaturePython)
  Placement = pos=(45.6,17.9213,82.882) rot=(0,1,0;1.5708rad)
  baseObject = -> Washer018 [Edge1]
  diameter = 4
  invert = false
  matchOuter = false
  offset = 0
  type = 4
FEATURE [Part::FeaturePython] Washer028  label="M3-Arandela034"  # Fasteners workbench fastener (typed FeaturePython)
  Placement = pos=(46.1,22.8388,101.235) rot=(0,1,0;1.5708rad)
  baseObject = -> Washer020 [Edge1]
  diameter = 4
  invert = false
  matchOuter = false
  offset = 0
  type = 4
FEATURE [Part::FeaturePython] Washer029  label="M3-Arandela035"  # Fasteners workbench fastener (typed FeaturePython)
  Placement = pos=(46.1,17.9213,82.882) rot=(0,1,0;1.5708rad)
  baseObject = -> Washer021 [Edge1]
  diameter = 4
  invert = false
  matchOuter = false
  offset = 0
  type = 4
FEATURE [Part::FeaturePython] Washer030  label="M3-Arandela036"  # Fasteners workbench fastener (typed FeaturePython)
  Placement = pos=(46.6,22.8388,101.235) rot=(0,1,0;1.5708rad)
  baseObject = -> Washer024 [Edge1]
  diameter = 4
  invert = false
  matchOuter = false
  offset = 0
  type = 4
FEATURE [Part::FeaturePython] Washer031  label="M3-Arandela037"  # Fasteners workbench fastener (typed FeaturePython)
  Placement = pos=(46.6,17.9213,82.882) rot=(0,1,0;1.5708rad)
  baseObject = -> Washer025 [Edge1]
  diameter = 4
  invert = false
  matchOuter = false
  offset = 0
  type = 4
FEATURE [Part::FeaturePython] b_Endstop1_001_001  label="Endstop1_002"  # a2plus imported part (geometry in sourceFile) (typed FeaturePython)
  Placement = pos=(47.1,23.7215,85.2102) rot=(0.704063,-0.092692,-0.704063;2.95674rad)
  a2p_Version = 0.4.60k
  fixedPosition = false
  objectType = a2pPart
  sourceFile = .\..\Complements\Endstop.step
  subassemblyImport = false
  timeLastImport = 1.68866e+09
  updateColors = true
FEATURE [App::FeaturePython] circularEdge_019  label="circularEdge_019__#8_MotorsPlateLeft_001"  # a2plus constraint (typed FeaturePython)
  Object1 = b_Endstop1_001_001
  Object2 = b__8_MotorsPlateLeft_001_
  ParentTreeObject = -> b_Endstop1_001_001
  SubElement1 = Edge459
  SubElement2 = Edge47
  Suppressed = false
  Type = circularEdge
  directionConstraint = 1
  lockRotation = false
  offset = 2
FEATURE [App::FeaturePython] circularEdge_019_mirror  label="circularEdge_019__Endstop1_002"  # a2plus constraint (typed FeaturePython)
  Object1 = b_Endstop1_001_001
  Object2 = b__8_MotorsPlateLeft_001_
  ParentTreeObject = -> b__8_MotorsPlateLeft_001_
  SubElement1 = Edge459
  SubElement2 = Edge47
  Suppressed = false
  Type = circularEdge
  directionConstraint = 1
  lockRotation = false
  offset = 2
FEATURE [Part::FeaturePython] Screw011  label="M3x12-Tornillo"  # Fasteners workbench fastener (typed FeaturePython)
  Placement = pos=(48.1,22.8388,101.235) rot=(0,1,0;1.5708rad)
  baseObject = -> b_Endstop1_001_001 [Edge451]
  diameter = 4
  invert = true
  leftHanded = false
  length = 10
  lengthCustom = 12
  matchOuter = false
  offset = 0
  thread = false
  type = 45
FEATURE [Part::FeaturePython] Screw012  label="M3x12-Tornillo001"  # Fasteners workbench fastener (typed FeaturePython)
  Placement = pos=(48.1,17.9213,82.882) rot=(0,1,0;1.5708rad)
  baseObject = -> b_Endstop1_001_001 [Edge450]
  diameter = 4
  invert = true
  leftHanded = false
  length = 10
  lengthCustom = 12
  matchOuter = false
  offset = 0
  thread = false
  type = 45
FEATURE [Part::FeaturePython] b__9_PasiveBearingSpacer_001_  label="#9_PasiveBearingSpacer_001"  # a2plus imported part (geometry in sourceFile) (typed FeaturePython)
  Placement = pos=(-35.1,8,53) rot=(0.706571,-0.038932,0.706571;3.21942rad)
  a2p_Version = 0.4.60k
  fixedPosition = false
  objectType = a2pPart
  sourceFile = .\#9_PasiveBearingSpacer.FCStd
  subassemblyImport = false
  timeLastImport = 1.68295e+09
  updateColors = true
FEATURE [App::FeaturePython] circularEdge_020  label="circularEdge_020__#7_MotorsPlateRight_001"  # a2plus constraint (typed FeaturePython)
  Object1 = b__9_PasiveBearingSpacer_001_
  Object2 = b__7_MotorsPlateRight_001_
  ParentTreeObject = -> b__9_PasiveBearingSpacer_001_
  SubElement1 = Edge2
  SubElement2 = Edge30
  Suppressed = false
  Type = circularEdge
  directionConstraint = 0
  lockRotation = false
  offset = 0
FEATURE [App::FeaturePython] circularEdge_020_mirror  label="circularEdge_020__#9_PasiveBearingSpacer_001"  # a2plus constraint (typed FeaturePython)
  Object1 = b__9_PasiveBearingSpacer_001_
  Object2 = b__7_MotorsPlateRight_001_
  ParentTreeObject = -> b__7_MotorsPlateRight_001_
  SubElement1 = Edge2
  SubElement2 = Edge30
  Suppressed = false
  Type = circularEdge
  directionConstraint = 0
  lockRotation = false
  offset = 0
FEATURE [Part::FeaturePython] b__9_PasiveBearingSpacer_001_001  label="#9_PasiveBearingSpacer_002"  # a2plus imported part (geometry in sourceFile) (typed FeaturePython)
  Placement = pos=(35.1,8,53) rot=(0.33368,-0.881655,-0.33368;1.69642rad)
  a2p_Version = 0.4.60k
  fixedPosition = false
  objectType = a2pPart
  sourceFile = .\#9_PasiveBearingSpacer.FCStd
  subassemblyImport = false
  timeLastImport = 1.68295e+09
  updateColors = true
FEATURE [App::FeaturePython] circularEdge_021  label="circularEdge_021__#8_MotorsPlateLeft_001"  # a2plus constraint (typed FeaturePython)
  Object1 = b__9_PasiveBearingSpacer_001_001
  Object2 = b__8_MotorsPlateLeft_001_
  ParentTreeObject = -> b__9_PasiveBearingSpacer_001_001
  SubElement1 = Edge2
  SubElement2 = Edge71
  Suppressed = false
  Type = circularEdge
  directionConstraint = 1
  lockRotation = false
  offset = 0
FEATURE [App::FeaturePython] circularEdge_021_mirror  label="circularEdge_021__#9_PasiveBearingSpacer_002"  # a2plus constraint (typed FeaturePython)
  Object1 = b__9_PasiveBearingSpacer_001_001
  Object2 = b__8_MotorsPlateLeft_001_
  ParentTreeObject = -> b__8_MotorsPlateLeft_001_
  SubElement1 = Edge2
  SubElement2 = Edge71
  Suppressed = false
  Type = circularEdge
  directionConstraint = 1
  lockRotation = false
  offset = 0
FEATURE [Part::FeaturePython] b_F6231_001_  label="F6231_001"  # a2plus imported part (geometry in sourceFile) (typed FeaturePython)
  Placement = pos=(-26.85,8,53) rot=(0,-1,0;1.5708rad)
  a2p_Version = 0.4.60k
  fixedPosition = false
  objectType = a2pPart
  sourceFile = .\..\Complements\F623.step
  subassemblyImport = false
  timeLastImport = 1.68866e+09
  updateColors = true
FEATURE [App::FeaturePython] circularEdge_022  label="circularEdge_022__#9_PasiveBearingSpacer_001"  # a2plus constraint (typed FeaturePython)
  Object1 = b_F6231_001_
  Object2 = b__9_PasiveBearingSpacer_001_
  ParentTreeObject = -> b_F6231_001_
  SubElement1 = Edge8
  SubElement2 = Edge5
  Suppressed = false
  Type = circularEdge
  directionConstraint = 0
  lockRotation = false
  offset = 0
FEATURE [App::FeaturePython] circularEdge_022_mirror  label="circularEdge_022__F6231_001"  # a2plus constraint (typed FeaturePython)
  Object1 = b_F6231_001_
  Object2 = b__9_PasiveBearingSpacer_001_
  ParentTreeObject = -> b__9_PasiveBearingSpacer_001_
  SubElement1 = Edge8
  SubElement2 = Edge5
  Suppressed = false
  Type = circularEdge
  directionConstraint = 0
  lockRotation = false
  offset = 0
FEATURE [Part::FeaturePython] Washer032  label="M3-Arandela038"  # Fasteners workbench fastener (typed FeaturePython)
  Placement = pos=(-26.85,8,53) rot=(0,1,0;1.5708rad)
  baseObject = -> b_F6231_001_ [Edge1]
  diameter = 4
  invert = false
  matchOuter = false
  offset = 0
  type = 4
FEATURE [Part::FeaturePython] b_F6231_001_001  label="F6231_002"  # a2plus imported part (geometry in sourceFile) (typed FeaturePython)
  Placement = pos=(-26.35,8,53) rot=(0.548415,0.631255,0.548415;2.01542rad)
  a2p_Version = 0.4.60k
  fixedPosition = false
  objectType = a2pPart
  sourceFile = .\..\Complements\F623.step
  subassemblyImport = false
  timeLastImport = 1.68866e+09
  updateColors = true
FEATURE [App::FeaturePython] circularEdge_023  label="circularEdge_023__F6231_001"  # a2plus constraint (typed FeaturePython)
  Object1 = b_F6231_001_001
  Object2 = b_F6231_001_
  ParentTreeObject = -> b_F6231_001_001
  SubElement1 = Edge6
  SubElement2 = Edge7
  Suppressed = false
  Type = circularEdge
  directionConstraint = 1
  lockRotation = false
  offset = 0.5
FEATURE [App::FeaturePython] circularEdge_023_mirror  label="circularEdge_023__F6231_002"  # a2plus constraint (typed FeaturePython)
  Object1 = b_F6231_001_001
  Object2 = b_F6231_001_
  ParentTreeObject = -> b_F6231_001_
  SubElement1 = Edge6
  SubElement2 = Edge7
  Suppressed = false
  Type = circularEdge
  directionConstraint = 1
  lockRotation = false
  offset = 0.5
FEATURE [Part::FeaturePython] b_F6231_001_002  label="F6231_003"  # a2plus imported part (geometry in sourceFile) (typed FeaturePython)
  Placement = pos=(26.35,8,53) rot=(-0.278458,-0.919197,0.278458;1.65495rad)
  a2p_Version = 0.4.60k
  fixedPosition = false
  objectType = a2pPart
  sourceFile = .\..\Complements\F623.step
  subassemblyImport = false
  timeLastImport = 1.68866e+09
  updateColors = true
FEATURE [Part::FeaturePython] b_F6231_001_003  label="F6231_004"  # a2plus imported part (geometry in sourceFile) (typed FeaturePython)
  Placement = pos=(26.85,8,53) rot=(-0.517645,0.68124,-0.517645;1.94554rad)
  a2p_Version = 0.4.60k
  fixedPosition = false
  objectType = a2pPart
  sourceFile = .\..\Complements\F623.step
  subassemblyImport = false
  timeLastImport = 1.68866e+09
  updateColors = true
FEATURE [App::FeaturePython] circularEdge_024  label="circularEdge_024__#9_PasiveBearingSpacer_002"  # a2plus constraint (typed FeaturePython)
  Object1 = b_F6231_001_003
  Object2 = b__9_PasiveBearingSpacer_001_001
  ParentTreeObject = -> b_F6231_001_003
  SubElement1 = Edge14
  SubElement2 = Edge7
  Suppressed = false
  Type = circularEdge
  directionConstraint = 0
  lockRotation = false
  offset = 0
FEATURE [App::FeaturePython] circularEdge_024_mirror  label="circularEdge_024__F6231_004"  # a2plus constraint (typed FeaturePython)
  Object1 = b_F6231_001_003
  Object2 = b__9_PasiveBearingSpacer_001_001
  ParentTreeObject = -> b__9_PasiveBearingSpacer_001_001
  SubElement1 = Edge14
  SubElement2 = Edge7
  Suppressed = false
  Type = circularEdge
  directionConstraint = 0
  lockRotation = false
  offset = 0
FEATURE [Part::FeaturePython] Washer033  label="M3-Arandela039"  # Fasteners workbench fastener (typed FeaturePython)
  Placement = pos=(26.85,8,53) rot=(0,-1,0;1.5708rad)
  baseObject = -> b_F6231_001_003 [Edge7]
  diameter = 4
  invert = true
  matchOuter = false
  offset = 0
  type = 4
FEATURE [App::FeaturePython] circularEdge_025  label="circularEdge_025__F6231_004"  # a2plus constraint (typed FeaturePython)
  Object1 = b_F6231_001_002
  Object2 = b_F6231_001_003
  ParentTreeObject = -> b_F6231_001_002
  SubElement1 = Edge7
  SubElement2 = Edge7
  Suppressed = false
  Type = circularEdge
  directionConstraint = 1
  lockRotation = false
  offset = 0.5
FEATURE [App::FeaturePython] circularEdge_025_mirror  label="circularEdge_025__F6231_003"  # a2plus constraint (typed FeaturePython)
  Object1 = b_F6231_001_002
  Object2 = b_F6231_001_003
  ParentTreeObject = -> b_F6231_001_003
  SubElement1 = Edge7
  SubElement2 = Edge7
  Suppressed = false
  Type = circularEdge
  directionConstraint = 1
  lockRotation = false
  offset = 0.5
FEATURE [Part::FeaturePython] Screw013  label="M3x20-Tornillo002"  # Fasteners workbench fastener (typed FeaturePython)
  Placement = pos=(22.35,8,53) rot=(0,-1,0;1.5708rad)
  baseObject = -> b_F6231_001_002 [Edge8]
  diameter = 4
  invert = false
  leftHanded = false
  length = 10
  lengthCustom = 20
  matchOuter = false
  offset = 0
  thread = false
  type = 45
FEATURE [Part::FeaturePython] Screw014  label="M3x20-Tornillo003"  # Fasteners workbench fastener (typed FeaturePython)
  Placement = pos=(-22.35,8,53) rot=(0,1,0;1.5708rad)
  baseObject = -> b_F6231_001_001 [Edge16]
  diameter = 4
  invert = true
  leftHanded = false
  length = 10
  lengthCustom = 20
  matchOuter = false
  offset = 0
  thread = false
  type = 45
